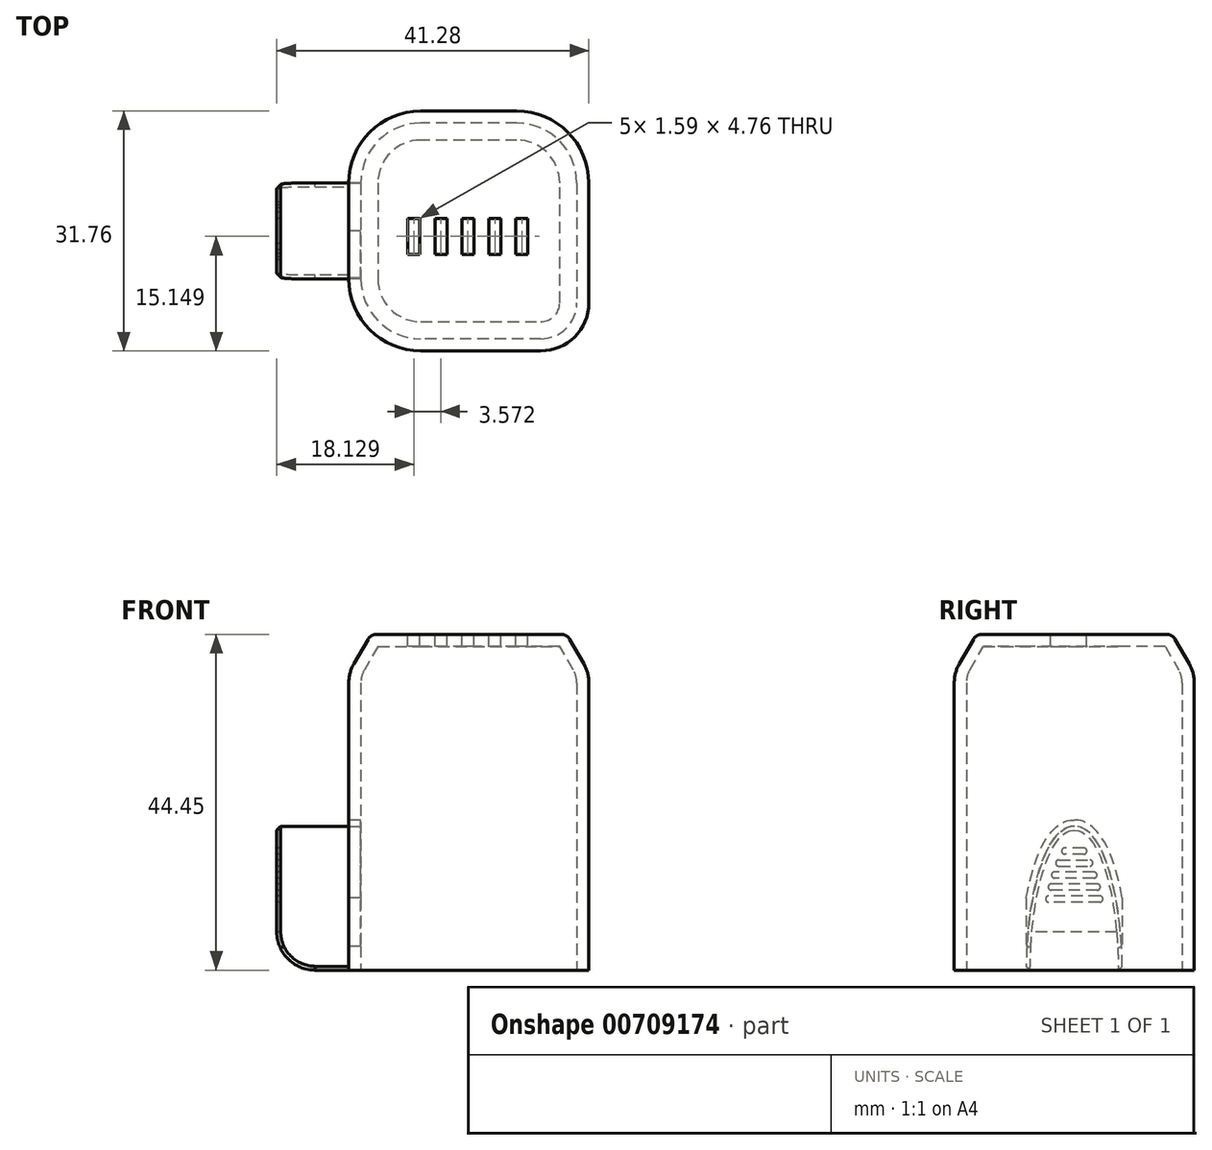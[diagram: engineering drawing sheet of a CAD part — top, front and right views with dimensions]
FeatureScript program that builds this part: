
annotation { "Feature Type Name" : "Feature", "Feature Type Description" : "" }
export const myFeature = defineFeature(function(context is Context, id is Id, definition is map)
    precondition{}
    {
        {
            var Q0;
            Q0=qCreatedBy(makeId("Top.planeOp"),FACE);
            var sketch = newSketch(context, id + "F0", { "sketchPlane" : qUnion([Q0])});
            skLineSegment(sketch, "E0.bottom", {"start": v(6.35, 15.88) * mm, "end": v(-6.35, 15.88) * mm});
            skLineSegment(sketch, "E0.top", {"start": v(9.52, -15.88) * mm, "end": v(-6.35, -15.88) * mm});
            skLineSegment(sketch, "E0.left", {"start": v(15.88, 6.35) * mm, "end": v(15.88, -9.52) * mm});
            skLineSegment(sketch, "E0.right", {"start": v(-15.88, 6.35) * mm, "end": v(-15.88, -6.35) * mm});
            skPoint(sketch, "E0.middle", {"position": v(0, 0) * mm});
            skPoint(sketch, "E1.visualSharp", {"position": v(-15.88, 15.88) * mm});
            skArc(sketch, "E1.filletArc", {"start": v(-6.35, 15.88) * mm, "mid": v(-13.09, 13.09) * mm, "end": v(-15.88, 6.35) * mm});
            skPoint(sketch, "E2.visualSharp", {"position": v(-15.88, -15.88) * mm});
            skArc(sketch, "E2.filletArc", {"start": v(-15.88, -6.35) * mm, "mid": v(-13.09, -13.09) * mm, "end": v(-6.35, -15.88) * mm});
            skPoint(sketch, "E3.visualSharp", {"position": v(15.88, 15.88) * mm});
            skArc(sketch, "E3.filletArc", {"start": v(15.88, 6.35) * mm, "mid": v(13.09, 13.09) * mm, "end": v(6.35, 15.88) * mm});
            skPoint(sketch, "E4.visualSharp", {"position": v(15.88, -15.88) * mm});
            skArc(sketch, "E4.filletArc", {"start": v(9.52, -15.88) * mm, "mid": v(14.02, -14.02) * mm, "end": v(15.88, -9.52) * mm});
            skSolve(sketch);
        }
        {
            var Q0;
            Q0=makeQuery(id+"F0.imprint","IMPRINT",FACE,{"disambiguationData":[TD([[makeQuery(id+"F0.imprint","IMPRINT",EDGE,{"derivedFrom":sQuery(id+"F0.wireOp",EDGE,"E0.bottom")}),1.0]])]});
            extrude(context, id + "F1", {"entities" : qUnion([Q0]), "depth" : 44.45 * mm, "offsetDistance" : 25.4 * mm});
        }
        {
            var Q0;
            Q0=makeQuery(id+"F1.opExtrude","CAP_FACE",FACE,{"disambiguationData":[OSD([sQuery(id+"F0.wireOp",EDGE,"E0.bottom"),sQuery(id+"F0.wireOp",EDGE,"E0.top"),sQuery(id+"F0.wireOp",EDGE,"E0.left"),sQuery(id+"F0.wireOp",EDGE,"E0.right"),sQuery(id+"F0.wireOp",EDGE,"E1.filletArc"),sQuery(id+"F0.wireOp",EDGE,"E2.filletArc"),sQuery(id+"F0.wireOp",EDGE,"E3.filletArc"),sQuery(id+"F0.wireOp",EDGE,"E4.filletArc")])],"isStart":false});
            chamfer(context, id + "F2", {"entities" : qUnion([Q0]), "chamferType" : ChamferType.OFFSET_ANGLE, "width" : 5.08 * mm, "oppositeDirection" : true, "angle" : 30 * degree, "tangentPropagation" : true});
        }
        {
            var Q0;
            Q0=makeQuery(id+"F1.opExtrude","CAP_FACE",FACE,{"disambiguationData":[OSD([sQuery(id+"F0.wireOp",EDGE,"E0.bottom"),sQuery(id+"F0.wireOp",EDGE,"E0.top"),sQuery(id+"F0.wireOp",EDGE,"E0.left"),sQuery(id+"F0.wireOp",EDGE,"E0.right"),sQuery(id+"F0.wireOp",EDGE,"E1.filletArc"),sQuery(id+"F0.wireOp",EDGE,"E2.filletArc"),sQuery(id+"F0.wireOp",EDGE,"E3.filletArc"),sQuery(id+"F0.wireOp",EDGE,"E4.filletArc")])],"isStart":false});
            fillet(context, id + "F3", {"entities" : qUnion([Q0]), "radius" : 1.27 * mm, "tangentPropagation" : true, "allowEdgeOverflow" : false});
        }
        {
            var Q0;
            {var subQ0=sQuery(id+"F0.wireOp",EDGE,"E0.top");Q0=makeQuery(id+"F2.opChamfer","BLEND_EDGE",EDGE,{"blendedFrom":[makeQuery(id+"F1.opExtrude","CAP_EDGE",EDGE,{"disambiguationData":[OSD([subQ0])],"isStart":false}),makeQuery(id+"F1.opExtrude","SWEPT_FACE",FACE,{"disambiguationData":[OSD([subQ0])]})],"blendedInto":[makeQuery(id+"F1.opExtrude","SWEPT_FACE",FACE,{"disambiguationData":[OSD([subQ0])]})]});}
            fillet(context, id + "F4", {"entities" : qUnion([Q0]), "radius" : 5.08 * mm, "tangentPropagation" : true, "allowEdgeOverflow" : false});
        }
        {
            var Q0;
            Q0=makeQuery(id+"F1.opExtrude","CAP_FACE",FACE,{"disambiguationData":[OSD([sQuery(id+"F0.wireOp",EDGE,"E0.bottom"),sQuery(id+"F0.wireOp",EDGE,"E0.top"),sQuery(id+"F0.wireOp",EDGE,"E0.left"),sQuery(id+"F0.wireOp",EDGE,"E0.right"),sQuery(id+"F0.wireOp",EDGE,"E1.filletArc"),sQuery(id+"F0.wireOp",EDGE,"E2.filletArc"),sQuery(id+"F0.wireOp",EDGE,"E3.filletArc"),sQuery(id+"F0.wireOp",EDGE,"E4.filletArc")])],"isStart":false});
            var sketch = newSketch(context, id + "F5", { "sketchPlane" : qUnion([Q0])});
            skLineSegment(sketch, "E5.bottom", {"start": v(-9.65, -3.9) * mm, "end": v(9.4, -3.9) * mm});
            skLineSegment(sketch, "E5.top", {"start": v(-9.65, 2.44) * mm, "end": v(9.4, 2.44) * mm});
            skLineSegment(sketch, "E5.left", {"start": v(-9.65, -3.9) * mm, "end": v(-9.65, 2.44) * mm});
            skLineSegment(sketch, "E5.right", {"start": v(9.4, -3.9) * mm, "end": v(9.4, 2.44) * mm});
            skLineSegment(sketch, "E6.bottom", {"start": v(-8.06, 1.65) * mm, "end": v(-6.48, 1.65) * mm});
            skLineSegment(sketch, "E6.top", {"start": v(-8.06, -3.11) * mm, "end": v(-6.48, -3.11) * mm});
            skLineSegment(sketch, "E6.left", {"start": v(-8.06, 1.65) * mm, "end": v(-8.06, -3.11) * mm});
            skLineSegment(sketch, "E6.right", {"start": v(-6.48, 1.65) * mm, "end": v(-6.48, -3.11) * mm});
            skLineSegment(sketch, "E7", {"start": v(-9.65, -0.73) * mm, "end": v(9.4, -0.73) * mm, "construction": true});
            skPoint(sketch, "E8", {"position": v(-8.06, -0.73) * mm});
            skLineSegment(sketch, "E9.1.0.0", {"start": v(-4.5, 1.65) * mm, "end": v(-4.5, -3.11) * mm});
            skPoint(sketch, "E9.1.0.1", {"position": v(-4.5, -0.73) * mm});
            skLineSegment(sketch, "E9.1.0.2", {"start": v(-2.9, 1.65) * mm, "end": v(-2.9, -3.11) * mm});
            skLineSegment(sketch, "E9.1.0.3", {"start": v(-4.5, 1.65) * mm, "end": v(-2.9, 1.65) * mm});
            skLineSegment(sketch, "E9.1.0.4", {"start": v(-4.5, -3.11) * mm, "end": v(-2.9, -3.11) * mm});
            skLineSegment(sketch, "E9.2.0.0", {"start": v(-0.92, 1.65) * mm, "end": v(-0.92, -3.11) * mm});
            skPoint(sketch, "E9.2.0.1", {"position": v(-0.92, -0.73) * mm});
            skLineSegment(sketch, "E9.2.0.2", {"start": v(0.67, 1.65) * mm, "end": v(0.67, -3.11) * mm});
            skLineSegment(sketch, "E9.2.0.3", {"start": v(-0.92, 1.65) * mm, "end": v(0.67, 1.65) * mm});
            skLineSegment(sketch, "E9.2.0.4", {"start": v(-0.92, -3.11) * mm, "end": v(0.67, -3.11) * mm});
            skLineSegment(sketch, "E9.3.0.0", {"start": v(2.65, 1.65) * mm, "end": v(2.65, -3.11) * mm});
            skPoint(sketch, "E9.3.0.1", {"position": v(2.65, -0.73) * mm});
            skLineSegment(sketch, "E9.3.0.2", {"start": v(4.24, 1.65) * mm, "end": v(4.24, -3.11) * mm});
            skLineSegment(sketch, "E9.3.0.3", {"start": v(2.65, 1.65) * mm, "end": v(4.24, 1.65) * mm});
            skLineSegment(sketch, "E9.3.0.4", {"start": v(2.65, -3.11) * mm, "end": v(4.24, -3.11) * mm});
            skLineSegment(sketch, "E9.4.0.0", {"start": v(6.22, 1.65) * mm, "end": v(6.22, -3.11) * mm});
            skPoint(sketch, "E9.4.0.1", {"position": v(6.22, -0.73) * mm});
            skLineSegment(sketch, "E9.4.0.2", {"start": v(7.81, 1.65) * mm, "end": v(7.81, -3.11) * mm});
            skLineSegment(sketch, "E9.4.0.3", {"start": v(6.22, 1.65) * mm, "end": v(7.81, 1.65) * mm});
            skLineSegment(sketch, "E9.4.0.4", {"start": v(6.22, -3.11) * mm, "end": v(7.81, -3.11) * mm});
            skLineSegment(sketch, "E9.direction1", {"start": v(-8.06, -3.11) * mm, "end": v(-4.5, -3.11) * mm, "construction": true});
            skLineSegment(sketch, "E10", {"start": v(-0.13, 1.65) * mm, "end": v(-0.13, 2.44) * mm, "construction": true});
            skSolve(sketch);
        }
        {
            var Q0;
            Q0=makeQuery(id+"F1.opExtrude","CAP_FACE",FACE,{"disambiguationData":[OSD([sQuery(id+"F0.wireOp",EDGE,"E0.bottom"),sQuery(id+"F0.wireOp",EDGE,"E0.top"),sQuery(id+"F0.wireOp",EDGE,"E0.left"),sQuery(id+"F0.wireOp",EDGE,"E0.right"),sQuery(id+"F0.wireOp",EDGE,"E1.filletArc"),sQuery(id+"F0.wireOp",EDGE,"E2.filletArc"),sQuery(id+"F0.wireOp",EDGE,"E3.filletArc"),sQuery(id+"F0.wireOp",EDGE,"E4.filletArc")])],"isStart":true});
            shell(context, id + "F6", {"entities" : qUnion([Q0]), "thickness" : 1.6 * mm});
        }
        {
            var Q0;
            Q0=makeQuery(id+"F5.imprint","IMPRINT",FACE,{"disambiguationData":[TD([[makeQuery(id+"F5.imprint","IMPRINT",EDGE,{"derivedFrom":sQuery(id+"F5.wireOp",EDGE,"E6.bottom")}),-1.0]])]});
            var Q1;
            Q1=makeQuery(id+"F5.imprint","IMPRINT",FACE,{"disambiguationData":[TD([[makeQuery(id+"F5.imprint","IMPRINT",EDGE,{"derivedFrom":sQuery(id+"F5.wireOp",EDGE,"E9.1.0.0")}),1.0]])]});
            var Q2;
            Q2=makeQuery(id+"F5.imprint","IMPRINT",FACE,{"disambiguationData":[TD([[makeQuery(id+"F5.imprint","IMPRINT",EDGE,{"derivedFrom":sQuery(id+"F5.wireOp",EDGE,"E9.2.0.0")}),1.0]])]});
            var Q3;
            Q3=makeQuery(id+"F5.imprint","IMPRINT",FACE,{"disambiguationData":[TD([[makeQuery(id+"F5.imprint","IMPRINT",EDGE,{"derivedFrom":sQuery(id+"F5.wireOp",EDGE,"E9.3.0.0")}),1.0]])]});
            var Q4;
            Q4=makeQuery(id+"F5.imprint","IMPRINT",FACE,{"disambiguationData":[TD([[makeQuery(id+"F5.imprint","IMPRINT",EDGE,{"derivedFrom":sQuery(id+"F5.wireOp",EDGE,"E9.4.0.0")}),1.0]])]});
            extrude(context, id + "F7", {"entities" : qUnion([Q0, Q1, Q2, Q3, Q4]), "operationType" : NewBodyOperationType.REMOVE, "endBound" : BoundingType.UP_TO_NEXT, "oppositeDirection" : true, "depth" : 25.4 * mm, "offsetDistance" : 25.4 * mm});
        }
        {
            var Q0;
            Q0=makeQuery(id+"F1.opExtrude","SWEPT_FACE",FACE,{"disambiguationData":[OSD([sQuery(id+"F0.wireOp",EDGE,"E0.right")])]});
            var sketch = newSketch(context, id + "F8", { "sketchPlane" : qUnion([Q0])});
            skLineSegment(sketch, "E11", {"start": v(-6.35, 0) * mm, "end": v(6.35, 0) * mm});
            skFitSpline(sketch, "E12", {"points": [v(-6.35, 0) * mm, v(0, 19.05) * mm], "startDerivative": vector(0, 24.94) * mm, "endDerivative": vector(12.88, 0) * mm});
            skFitSpline(sketch, "E13.MirrorCS", {"points": [v(6.35, 0) * mm, v(0, 19.05) * mm], "startDerivative": vector(0, 24.94) * mm, "endDerivative": vector(-12.88, 0) * mm});
            skFitSpline(sketch, "E14.0", {"points": [v(7.14, 0) * mm, v(7.14, 2.11) * mm, v(6.95, 5.5) * mm, v(6.29, 9.87) * mm, v(5.59, 12.92) * mm, v(4.67, 15.6) * mm, v(3.7, 17.44) * mm, v(2.77, 18.59) * mm, v(1.96, 19.27) * mm, v(1.04, 19.73) * mm, v(0.35, 19.84) * mm, v(0, 19.84) * mm]});
            skFitSpline(sketch, "E14.1", {"points": [v(-7.14, 0) * mm, v(-7.14, 2.11) * mm, v(-6.95, 5.5) * mm, v(-6.29, 9.87) * mm, v(-5.59, 12.92) * mm, v(-4.67, 15.6) * mm, v(-3.7, 17.44) * mm, v(-2.77, 18.59) * mm, v(-1.96, 19.27) * mm, v(-1.04, 19.73) * mm, v(-0.35, 19.84) * mm, v(0, 19.84) * mm]});
            skLineSegment(sketch, "E15", {"start": v(-7.05, 3.17) * mm, "end": v(-6.26, 3.17) * mm});
            skLineSegment(sketch, "E16", {"start": v(6.26, 3.18) * mm, "end": v(7.05, 3.18) * mm});
            skSolve(sketch);
        }
        {
            var Q0;
            {var subQ1=sQuery(id+"F8.wireOp",EDGE,"E11");Q0=makeQuery(id+"F8.imprint","IMPRINT",FACE,{"disambiguationData":[TD([[makeQuery(id+"F8.imprint","IMPRINT",EDGE,{"derivedFrom":subQ1}),1.0]])]});}
            extrude(context, id + "F9", {"entities" : qUnion([Q0]), "operationType" : NewBodyOperationType.ADD, "depth" : 9.52 * mm, "offsetDistance" : 25.4 * mm});
        }
        {
            var Q0;
            Q0=makeQuery(id+"F9.opExtrude","CAP_EDGE",EDGE,{"disambiguationData":[OSD([sQuery(id+"F8.wireOp",EDGE,"E11")])],"isStart":false});
            fillet(context, id + "F10", {"entities" : qUnion([Q0]), "radius" : 5.08 * mm, "tangentPropagation" : true, "allowEdgeOverflow" : false});
        }
        {
            var Q0;
            Q0=makeQuery(id+"F9.opExtrude","CAP_EDGE",EDGE,{"disambiguationData":[OSD([sQuery(id+"F8.wireOp",EDGE,"E12")])],"isStart":false});
            chamfer(context, id + "F11", {"entities" : qUnion([Q0]), "width" : 0.5 * mm, "tangentPropagation" : true});
        }
        {
            var Q0;
            {var subQ10=sQuery(id+"F8.wireOp",EDGE,"E13.MirrorCS");var subQ11=sQuery(id+"F8.wireOp",EDGE,"E12");var subQ12=makeQuery(id+"F8.imprint","INTERSECT",VERTEX,{"derivedFrom":[subQ11,subQ10]});Q0=makeQuery(id+"F8.imprint","IMPRINT",FACE,{"disambiguationData":[TD([[makeQuery(id+"F8.imprint","IMPRINT",EDGE,{"disambiguationData":[TD([[subQ12,1.0]])],"derivedFrom":subQ11}),1.0]])]});}
            var Q1;
            {var subQ0=sQuery(id+"F8.wireOp",EDGE,"E15");var subQ1=sQuery(id+"F8.wireOp",EDGE,"E14.1");var subQ2=makeQuery(id+"F8.imprint","INTERSECT",VERTEX,{"derivedFrom":[subQ1,subQ0]});Q1=makeQuery(id+"F8.imprint","IMPRINT",FACE,{"disambiguationData":[TD([[makeQuery(id+"F8.imprint","IMPRINT",EDGE,{"disambiguationData":[TD([[subQ2,-1.0]])],"derivedFrom":subQ1}),-1.0]])]});}
            var Q2;
            {var subQ0=sQuery(id+"F8.wireOp",EDGE,"E16");var subQ1=sQuery(id+"F8.wireOp",EDGE,"E14.0");var subQ2=makeQuery(id+"F8.imprint","INTERSECT",VERTEX,{"derivedFrom":[subQ1,subQ0]});Q2=makeQuery(id+"F8.imprint","IMPRINT",FACE,{"disambiguationData":[TD([[makeQuery(id+"F8.imprint","IMPRINT",EDGE,{"disambiguationData":[TD([[subQ2,-1.0]])],"derivedFrom":subQ1}),1.0]])]});}
            extrude(context, id + "F12", {"entities" : qUnion([Q0, Q1, Q2]), "operationType" : NewBodyOperationType.REMOVE, "endBound" : BoundingType.UP_TO_NEXT, "oppositeDirection" : true, "depth" : 25.4 * mm, "offsetDistance" : 25.4 * mm});
        }
        {
            var Q0;
            Q0=makeQuery(id+"F9.opExtrude","CAP_FACE",FACE,{"disambiguationData":[OSD([sQuery(id+"F8.wireOp",EDGE,"E11"),sQuery(id+"F8.wireOp",EDGE,"E12"),sQuery(id+"F8.wireOp",EDGE,"E13.MirrorCS")])],"isStart":false});
            var sketch = newSketch(context, id + "F13", { "sketchPlane" : qUnion([Q0])});
            skLineSegment(sketch, "E17.0", {"start": v(-3.83, 6.67) * mm, "end": v(3.83, 6.67) * mm, "construction": true});
            skFitSpline(sketch, "E17.1", {"points": [v(-0.02, 16.95) * mm, v(-0.04, 16.95) * mm, v(-0.1, 16.95) * mm, v(-0.17, 16.93) * mm, v(-0.3, 16.87) * mm, v(-0.47, 16.75) * mm, v(-0.64, 16.6) * mm, v(-0.8, 16.42) * mm, v(-0.92, 16.27) * mm, v(-1.05, 16.1) * mm, v(-1.16, 15.93) * mm, v(-1.26, 15.79) * mm, v(-1.31, 15.7) * mm, v(-1.36, 15.62) * mm, v(-1.4, 15.56) * mm, v(-1.42, 15.5) * mm, v(-1.44, 15.47) * mm, v(-1.45, 15.45) * mm, v(-1.46, 15.44) * mm, v(-1.47, 15.43) * mm, v(-1.47, 15.42) * mm, v(-1.49, 15.4) * mm, v(-1.5, 15.36) * mm, v(-1.52, 15.32) * mm, v(-1.55, 15.27) * mm, v(-1.59, 15.2) * mm, v(-1.64, 15.1) * mm, v(-1.7, 14.96) * mm, v(-1.8, 14.8) * mm, v(-1.87, 14.61) * mm, v(-1.98, 14.37) * mm, v(-2.12, 14.04) * mm, v(-2.28, 13.62) * mm, v(-2.4, 13.25) * mm, v(-2.5, 12.94) * mm, v(-2.57, 12.74) * mm, v(-2.62, 12.58) * mm, v(-2.66, 12.45) * mm, v(-2.69, 12.35) * mm, v(-2.71, 12.27) * mm, v(-2.72, 12.23) * mm, v(-2.73, 12.2) * mm, v(-2.74, 12.18) * mm, v(-2.75, 12.14) * mm, v(-2.77, 12.09) * mm, v(-2.79, 12) * mm, v(-2.81, 11.9) * mm, v(-2.85, 11.78) * mm, v(-2.9, 11.61) * mm, v(-2.96, 11.35) * mm, v(-3.05, 11.01) * mm, v(-3.15, 10.6) * mm, v(-3.24, 10.17) * mm, v(-3.36, 9.6) * mm, v(-3.5, 8.86) * mm, v(-3.66, 7.93) * mm, v(-3.84, 6.65) * mm, v(-3.95, 5.63) * mm, v(-4.02, 4.93) * mm], "construction": true});
            skFitSpline(sketch, "E17.2", {"points": [v(4.02, 4.93) * mm, v(3.95, 5.63) * mm, v(3.84, 6.64) * mm, v(3.66, 7.92) * mm, v(3.5, 8.84) * mm, v(3.36, 9.58) * mm, v(3.24, 10.16) * mm, v(3.15, 10.58) * mm, v(3.05, 11) * mm, v(2.97, 11.33) * mm, v(2.9, 11.6) * mm, v(2.85, 11.76) * mm, v(2.82, 11.9) * mm, v(2.8, 12) * mm, v(2.77, 12.07) * mm, v(2.75, 12.13) * mm, v(2.74, 12.16) * mm, v(2.74, 12.18) * mm, v(2.73, 12.21) * mm, v(2.72, 12.26) * mm, v(2.7, 12.33) * mm, v(2.66, 12.43) * mm, v(2.63, 12.56) * mm, v(2.58, 12.72) * mm, v(2.51, 12.92) * mm, v(2.41, 13.23) * mm, v(2.28, 13.6) * mm, v(2.12, 14.02) * mm, v(1.96, 14.41) * mm, v(1.83, 14.71) * mm, v(1.72, 14.94) * mm, v(1.65, 15.08) * mm, v(1.6, 15.2) * mm, v(1.55, 15.27) * mm, v(1.52, 15.33) * mm, v(1.5, 15.38) * mm, v(1.48, 15.4) * mm, v(1.47, 15.42) * mm, v(1.46, 15.45) * mm, v(1.44, 15.48) * mm, v(1.4, 15.53) * mm, v(1.36, 15.61) * mm, v(1.3, 15.7) * mm, v(1.23, 15.82) * mm, v(1.14, 15.96) * mm, v(1.04, 16.11) * mm, v(0.95, 16.23) * mm, v(0.88, 16.31) * mm, v(0.84, 16.36) * mm, v(0.8, 16.4) * mm, v(0.8, 16.42) * mm, v(0.77, 16.44) * mm, v(0.74, 16.47) * mm, v(0.7, 16.52) * mm, v(0.64, 16.58) * mm, v(0.52, 16.7) * mm, v(0.35, 16.83) * mm, v(0.19, 16.92) * mm, v(0.09, 16.95) * mm, v(0.05, 16.95) * mm, v(0.02, 16.95) * mm], "construction": true});
            skLineSegment(sketch, "E18", {"start": v(-1.27, 15.76) * mm, "end": v(1.27, 15.76) * mm});
            skLineSegment(sketch, "E19", {"start": v(0, 15.76) * mm, "end": v(0, 14.17) * mm, "construction": true});
            skLineSegment(sketch, "E20", {"start": v(0, 14.17) * mm, "end": v(0, 12.58) * mm, "construction": true});
            skLineSegment(sketch, "E21", {"start": v(0, 12.58) * mm, "end": v(0, 11) * mm, "construction": true});
            skLineSegment(sketch, "E22", {"start": v(0, 11) * mm, "end": v(0, 9.4) * mm, "construction": true});
            skLineSegment(sketch, "E23", {"start": v(2.06, 14.17) * mm, "end": v(-2.06, 14.17) * mm});
            skLineSegment(sketch, "E24", {"start": v(-2.62, 12.58) * mm, "end": v(2.62, 12.58) * mm});
            skLineSegment(sketch, "E25", {"start": v(-3.05, 11) * mm, "end": v(3.05, 11) * mm});
            skLineSegment(sketch, "E26", {"start": v(-3.4, 9.4) * mm, "end": v(3.4, 9.4) * mm});
            skArc(sketch, "E27.0.startCap", {"start": v(-1.27, 15.36) * mm, "mid": v(-1.67, 15.76) * mm, "end": v(-1.27, 16.16) * mm});
            skArc(sketch, "E27.0.endCap", {"start": v(1.27, 16.16) * mm, "mid": v(1.67, 15.76) * mm, "end": v(1.27, 15.36) * mm});
            skLineSegment(sketch, "E27.0.left", {"start": v(-1.27, 16.16) * mm, "end": v(1.27, 16.16) * mm});
            skLineSegment(sketch, "E27.0.right", {"start": v(-1.27, 15.36) * mm, "end": v(1.27, 15.36) * mm});
            skArc(sketch, "E27.1.startCap", {"start": v(2.06, 14.57) * mm, "mid": v(2.46, 14.17) * mm, "end": v(2.06, 13.77) * mm});
            skArc(sketch, "E27.1.endCap", {"start": v(-2.06, 13.77) * mm, "mid": v(-2.46, 14.17) * mm, "end": v(-2.06, 14.57) * mm});
            skLineSegment(sketch, "E27.1.left", {"start": v(2.06, 13.77) * mm, "end": v(-2.06, 13.77) * mm});
            skLineSegment(sketch, "E27.1.right", {"start": v(2.06, 14.57) * mm, "end": v(-2.06, 14.57) * mm});
            skArc(sketch, "E27.2.startCap", {"start": v(-2.62, 12.19) * mm, "mid": v(-3.02, 12.58) * mm, "end": v(-2.62, 12.98) * mm});
            skArc(sketch, "E27.2.endCap", {"start": v(2.62, 12.98) * mm, "mid": v(3.02, 12.58) * mm, "end": v(2.62, 12.19) * mm});
            skLineSegment(sketch, "E27.2.left", {"start": v(-2.62, 12.98) * mm, "end": v(2.62, 12.98) * mm});
            skLineSegment(sketch, "E27.2.right", {"start": v(-2.62, 12.19) * mm, "end": v(2.62, 12.19) * mm});
            skArc(sketch, "E27.3.startCap", {"start": v(-3.05, 10.6) * mm, "mid": v(-3.45, 11) * mm, "end": v(-3.05, 11.4) * mm});
            skArc(sketch, "E27.3.endCap", {"start": v(3.05, 11.4) * mm, "mid": v(3.45, 11) * mm, "end": v(3.05, 10.6) * mm});
            skLineSegment(sketch, "E27.3.left", {"start": v(-3.05, 11.4) * mm, "end": v(3.05, 11.4) * mm});
            skLineSegment(sketch, "E27.3.right", {"start": v(-3.05, 10.6) * mm, "end": v(3.05, 10.6) * mm});
            skArc(sketch, "E27.4.startCap", {"start": v(-3.4, 9.01) * mm, "mid": v(-3.8, 9.4) * mm, "end": v(-3.4, 9.8) * mm});
            skArc(sketch, "E27.4.endCap", {"start": v(3.4, 9.8) * mm, "mid": v(3.8, 9.4) * mm, "end": v(3.4, 9.01) * mm});
            skLineSegment(sketch, "E27.4.left", {"start": v(-3.4, 9.8) * mm, "end": v(3.4, 9.8) * mm});
            skLineSegment(sketch, "E27.4.right", {"start": v(-3.4, 9.01) * mm, "end": v(3.4, 9.01) * mm});
            skSolve(sketch);
        }
        {
            var Q0;
            Q0=makeQuery(id+"F13.imprint","IMPRINT",FACE,{"disambiguationData":[TD([[makeQuery(id+"F13.imprint","IMPRINT",EDGE,{"derivedFrom":sQuery(id+"F13.wireOp",EDGE,"E27.0.startCap")}),-1.0]])]});
            var Q1;
            Q1=makeQuery(id+"F13.imprint","IMPRINT",FACE,{"disambiguationData":[TD([[makeQuery(id+"F13.imprint","IMPRINT",EDGE,{"derivedFrom":sQuery(id+"F13.wireOp",EDGE,"E27.1.startCap")}),-1.0]])]});
            var Q2;
            Q2=makeQuery(id+"F13.imprint","IMPRINT",FACE,{"disambiguationData":[TD([[makeQuery(id+"F13.imprint","IMPRINT",EDGE,{"derivedFrom":sQuery(id+"F13.wireOp",EDGE,"E27.2.startCap")}),-1.0]])]});
            var Q3;
            Q3=makeQuery(id+"F13.imprint","IMPRINT",FACE,{"disambiguationData":[TD([[makeQuery(id+"F13.imprint","IMPRINT",EDGE,{"derivedFrom":sQuery(id+"F13.wireOp",EDGE,"E27.3.startCap")}),-1.0]])]});
            var Q4;
            Q4=makeQuery(id+"F13.imprint","IMPRINT",FACE,{"disambiguationData":[TD([[makeQuery(id+"F13.imprint","IMPRINT",EDGE,{"derivedFrom":sQuery(id+"F13.wireOp",EDGE,"E27.4.startCap")}),-1.0]])]});
            extrude(context, id + "F14", {"entities" : qUnion([Q0, Q1, Q2, Q3, Q4]), "operationType" : NewBodyOperationType.REMOVE, "oppositeDirection" : true, "depth" : 0.4 * mm, "offsetDistance" : 25.4 * mm});
        }
    });
